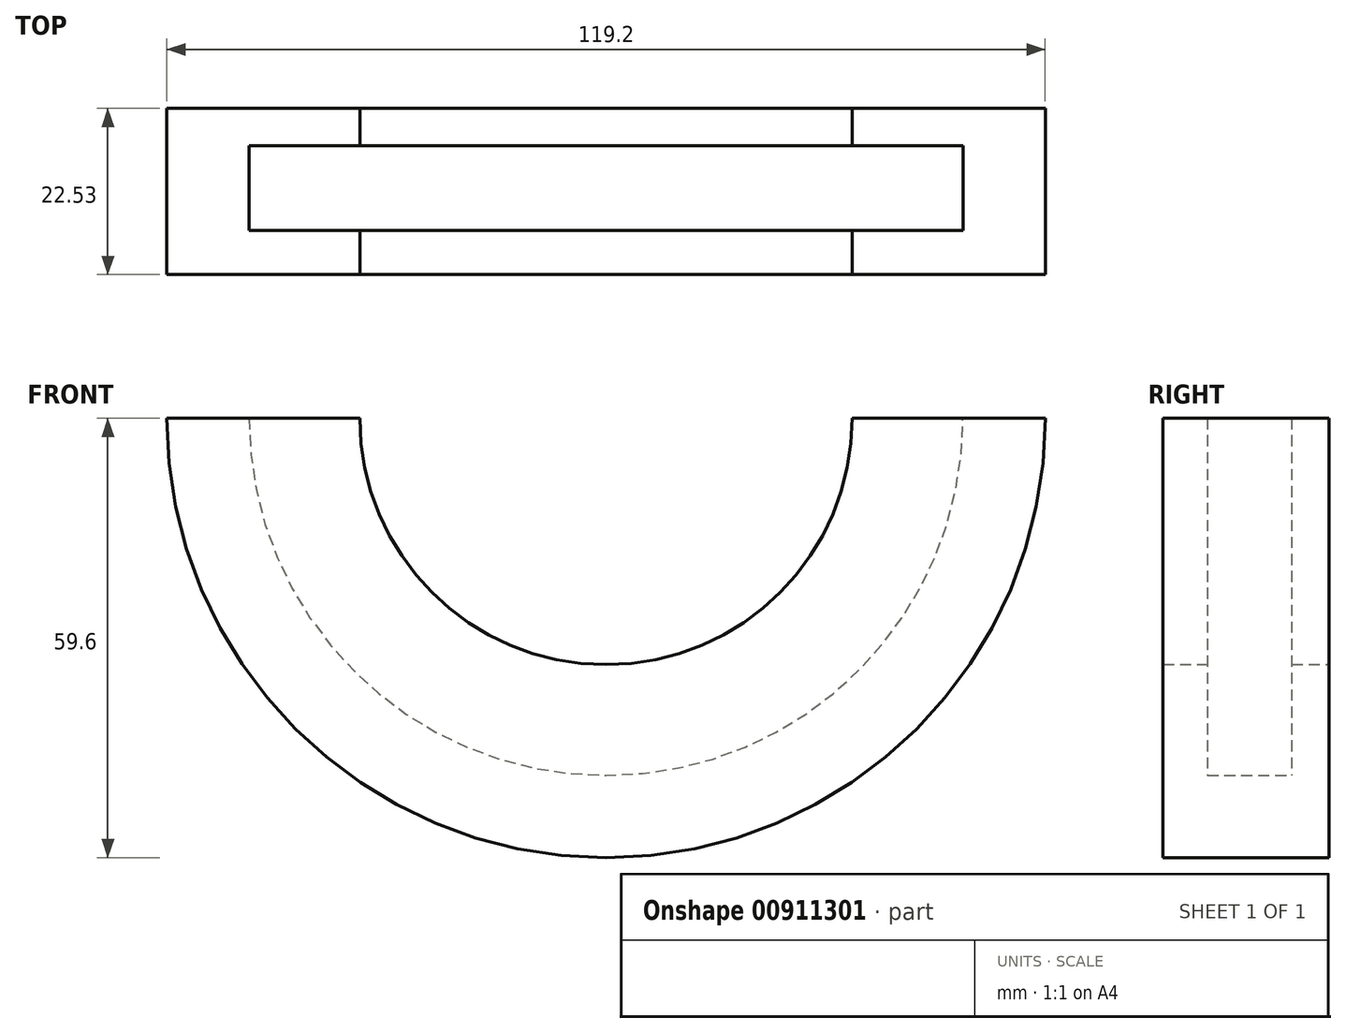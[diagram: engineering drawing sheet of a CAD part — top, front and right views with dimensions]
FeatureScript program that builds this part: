
annotation { "Feature Type Name" : "Feature", "Feature Type Description" : "" }
export const myFeature = defineFeature(function(context is Context, id is Id, definition is map)
    precondition{}
    {
        {
            var Q0;
            Q0=qCreatedBy(makeId("Top.planeOp"),FACE);
            var sketch = newSketch(context, id + "F0", { "sketchPlane" : qUnion([Q0])});
            skLineSegment(sketch, "E0.bottom", {"start": v(0, 22.53) * mm, "end": v(26.19, 22.53) * mm});
            skLineSegment(sketch, "E0.top", {"start": v(0, 0) * mm, "end": v(26.19, 0) * mm});
            skLineSegment(sketch, "E0.left", {"start": v(0, 22.53) * mm, "end": v(0, 0) * mm});
            skLineSegment(sketch, "E0.right", {"start": v(26.19, 22.53) * mm, "end": v(26.19, 17.46) * mm});
            skLineSegment(sketch, "E1", {"start": v(26.19, 17.46) * mm, "end": v(11.17, 17.46) * mm});
            skLineSegment(sketch, "E2", {"start": v(11.17, 17.46) * mm, "end": v(11.17, 6) * mm});
            skLineSegment(sketch, "E3", {"start": v(11.17, 6) * mm, "end": v(26.19, 6) * mm});
            skLineSegment(sketch, "E4.trimOffspring", {"start": v(26.19, 6) * mm, "end": v(26.19, 0) * mm});
            skLineSegment(sketch, "E5", {"start": v(59.6, 31.54) * mm, "end": v(59.6, -17.46) * mm, "construction": true});
            skSolve(sketch);
        }
        {
            var Q0;
            Q0=makeQuery(id+"F0.imprint","IMPRINT",FACE,{"disambiguationData":[TD([[makeQuery(id+"F0.imprint","IMPRINT",EDGE,{"derivedFrom":sQuery(id+"F0.wireOp",EDGE,"E0.bottom")}),-1.0]])]});
            var Q1;
            Q1=sQuery(id+"F0.wireOp",EDGE,"E5");
            revolve(context, id + "F1", {"surfaceOperationType" : NewSurfaceOperationType.NEW, "entities" : qUnion([Q0]), "axis" : qUnion([Q1]), "revolveType" : RevolveType.ONE_DIRECTION, "angle" : 180 * degree});
        }
    });
